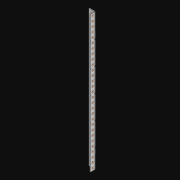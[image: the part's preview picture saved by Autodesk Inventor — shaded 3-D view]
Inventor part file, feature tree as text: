
AUTODESK INVENTOR PART (.ipt)
format: ipt  version: 2021 (Build 250183000, 183)  size: 1,293,824 bytes
history: native  units: in
note: dims shown in document units (in); Inventor stores cm internally (conversion verified against a paired STEP export)
features: extrude x60, other x58, sketch x4, pattern_linear x2, sheet_metal_op x1
ambient origin geometry x8: Origin, YZ Plane, XZ Plane, XY Plane, X Axis, Y Axis, Z Axis, Center Point
bodies: Solid1 (feature_tree)
feature tree (125):
  pattern_linear  "Rectangular Pattern1"  Spacing1=0.5in  [1 undecoded]
  pattern_linear  "Rectangular Pattern3"  Count1=29  [1 undecoded]
  extrude  "Extrusion1"  Depth=0.5in
  extrude  "Extrusion2"  Depth=0.5in
  sketch  "Sketch1"  dims[d0=0.182in]
  other  "Srf1"
  sketch  "Sketch3"  dims[d1=0.063in d2=0.0in]
  other  "Srf3"
  other  "Srf4"
  other  "Srf5"
  other  "Srf6"
  other  "Srf7"
  other  "Srf8"
  other  "Srf9"
  other  "Srf10"
  other  "Srf11"
  other  "Srf12"
  other  "Srf13"
  other  "Srf14"
  other  "Srf15"
  other  "Srf16"
  other  "Srf17"
  other  "Srf18"
  other  "Srf19"
  other  "Srf20"
  other  "Srf21"
  other  "Srf22"
  other  "Srf23"
  other  "Srf24"
  other  "Srf25"
  other  "Srf26"
  other  "Srf27"
  other  "Srf28"
  other  "Srf29"
  other  "Srf30"
  other  "Srf31"
  other  "Srf142"
  other  "Srf143"
  other  "Srf144"
  other  "Srf145"
  other  "Srf146"
  other  "Srf147"
  other  "Srf148"
  other  "Srf149"
  other  "Srf150"
  other  "Srf151"
  other  "Srf152"
  other  "Srf153"
  other  "Srf154"
  other  "Srf155"
  other  "Srf156"
  other  "Srf157"
  other  "Srf158"
  other  "Srf159"
  other  "Srf160"
  other  "Srf161"
  other  "Srf162"
  other  "Srf163"
  other  "Srf164"
  other  "Srf165"
  other  "Srf166"
  other  "Srf167"
  other  "Srf168"
  other  "Srf169"
  sketch  "Sketch4"  dims[d6=0.182in]
  sketch  "Sketch5"  dims[d7=0.063in d8=0.0in d11=0.5in d12=0.3937in d14=0.5in d18=11.4173in d20=0.5in d21=3.0in d22=0.0in d23=0.841in d24=0.0in]
  sheet_metal_op  "Fold1"
  extrude  "ExtrusionSrf1"  TaperAngle=0.0deg  [1 undecoded]
  extrude  "ExtrusionSrf3"  Depth=0.5in TaperAngle=0.0deg
  extrude  "ExtrusionSrf4"  [1 undecoded]
  extrude  "ExtrusionSrf5"  [1 undecoded]
  extrude  "ExtrusionSrf6"  [1 undecoded]
  extrude  "ExtrusionSrf7"  [1 undecoded]
  extrude  "ExtrusionSrf8"  [1 undecoded]
  extrude  "ExtrusionSrf9"  [1 undecoded]
  extrude  "ExtrusionSrf10"  [1 undecoded]
  extrude  "ExtrusionSrf11"  [1 undecoded]
  extrude  "ExtrusionSrf12"  [1 undecoded]
  extrude  "ExtrusionSrf13"  [1 undecoded]
  extrude  "ExtrusionSrf14"  [1 undecoded]
  extrude  "ExtrusionSrf15"  [1 undecoded]
  extrude  "ExtrusionSrf16"  [1 undecoded]
  extrude  "ExtrusionSrf17"  [1 undecoded]
  extrude  "ExtrusionSrf18"  [1 undecoded]
  extrude  "ExtrusionSrf19"  [1 undecoded]
  extrude  "ExtrusionSrf20"  [1 undecoded]
  extrude  "ExtrusionSrf21"  [1 undecoded]
  extrude  "ExtrusionSrf22"  [1 undecoded]
  extrude  "ExtrusionSrf23"  [1 undecoded]
  extrude  "ExtrusionSrf24"  [1 undecoded]
  extrude  "ExtrusionSrf25"  [1 undecoded]
  extrude  "ExtrusionSrf26"  [1 undecoded]
  extrude  "ExtrusionSrf27"  [1 undecoded]
  extrude  "ExtrusionSrf28"  [1 undecoded]
  extrude  "ExtrusionSrf29"  [1 undecoded]
  extrude  "ExtrusionSrf30"  [1 undecoded]
  extrude  "ExtrusionSrf31"  [1 undecoded]
  extrude  "ExtrusionSrf142"  [1 undecoded]
  extrude  "ExtrusionSrf143"  [1 undecoded]
  extrude  "ExtrusionSrf144"  [1 undecoded]
  extrude  "ExtrusionSrf145"  [1 undecoded]
  extrude  "ExtrusionSrf146"  [1 undecoded]
  extrude  "ExtrusionSrf147"  [1 undecoded]
  extrude  "ExtrusionSrf148"  [1 undecoded]
  extrude  "ExtrusionSrf149"  [1 undecoded]
  extrude  "ExtrusionSrf150"  [1 undecoded]
  extrude  "ExtrusionSrf151"  [1 undecoded]
  extrude  "ExtrusionSrf152"  [1 undecoded]
  extrude  "ExtrusionSrf153"  [1 undecoded]
  extrude  "ExtrusionSrf154"  [1 undecoded]
  extrude  "ExtrusionSrf155"  [1 undecoded]
  extrude  "ExtrusionSrf156"  [1 undecoded]
  extrude  "ExtrusionSrf157"  [1 undecoded]
  extrude  "ExtrusionSrf158"  [1 undecoded]
  extrude  "ExtrusionSrf159"  [1 undecoded]
  extrude  "ExtrusionSrf160"  [1 undecoded]
  extrude  "ExtrusionSrf161"  [1 undecoded]
  extrude  "ExtrusionSrf162"  [1 undecoded]
  extrude  "ExtrusionSrf163"  [1 undecoded]
  extrude  "ExtrusionSrf164"  [1 undecoded]
  extrude  "ExtrusionSrf165"  [1 undecoded]
  extrude  "ExtrusionSrf166"  [1 undecoded]
  extrude  "ExtrusionSrf167"  [1 undecoded]
  extrude  "ExtrusionSrf168"  [1 undecoded]
  extrude  "ExtrusionSrf169"  [1 undecoded]
note: 59 required parameter values undecoded (feature->parameter linkage not recoverable at this tier; creation-order binding heuristic only, values carry confidence <= 0.55)
